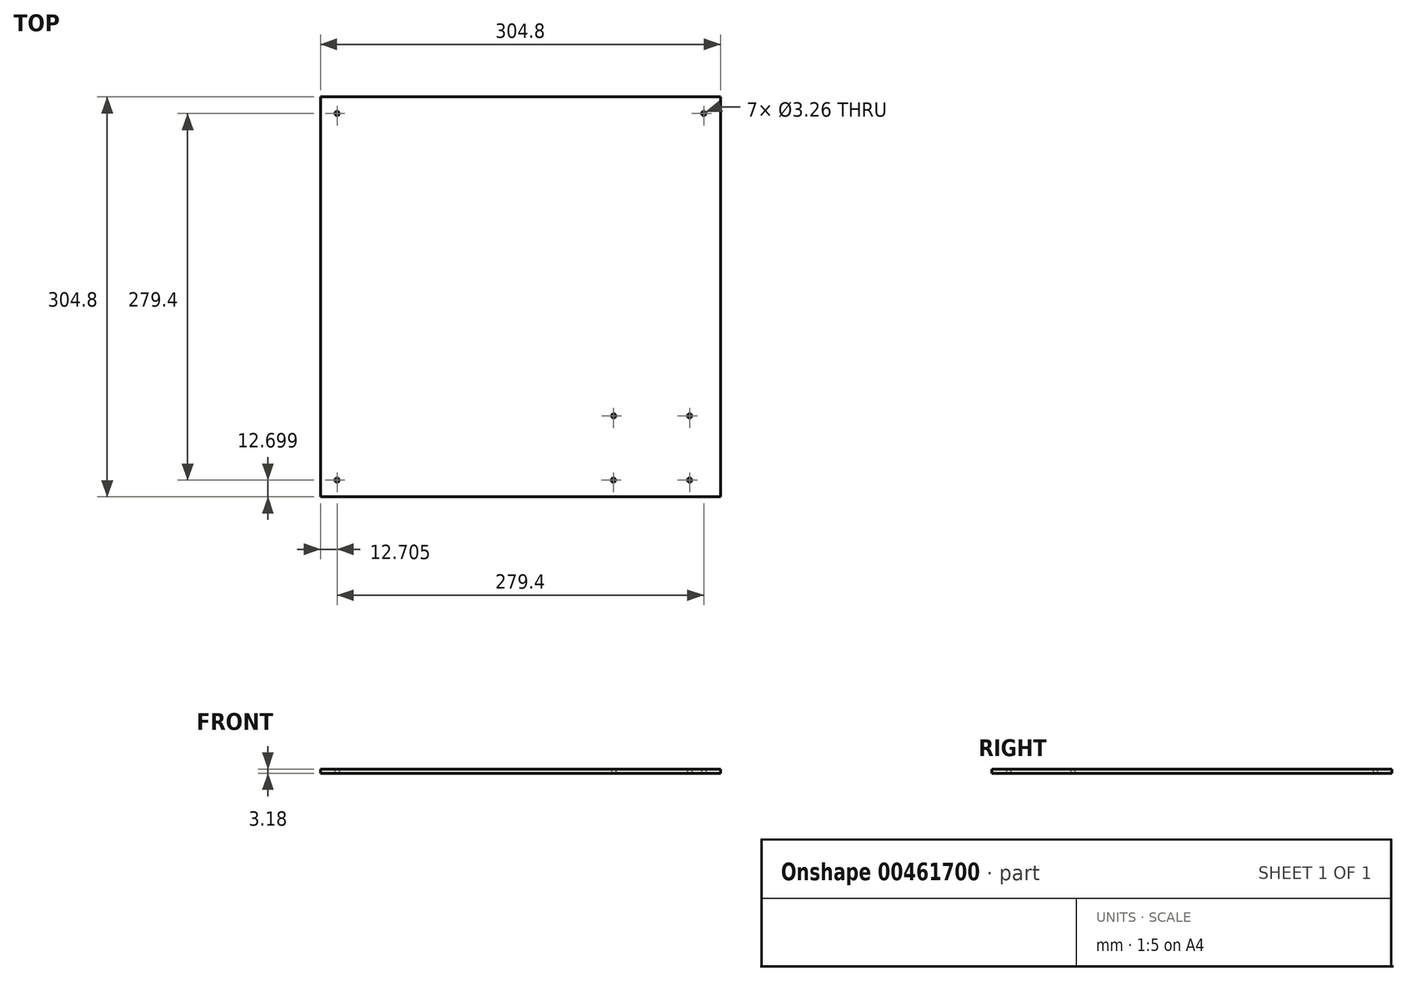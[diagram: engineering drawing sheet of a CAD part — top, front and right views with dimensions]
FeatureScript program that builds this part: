
annotation { "Feature Type Name" : "Feature", "Feature Type Description" : "" }
export const myFeature = defineFeature(function(context is Context, id is Id, definition is map)
    precondition{}
    {
        {
            var Q0;
            Q0=qCreatedBy(makeId("Top.planeOp"),FACE);
            var sketch = newSketch(context, id + "F0", { "sketchPlane" : qUnion([Q0])});
            skLineSegment(sketch, "E0.bottom", {"start": v(-241.1, 248.87) * mm, "end": v(63.7, 248.87) * mm});
            skLineSegment(sketch, "E0.top", {"start": v(-241.1, -55.93) * mm, "end": v(63.7, -55.93) * mm});
            skLineSegment(sketch, "E0.left", {"start": v(-241.1, 248.87) * mm, "end": v(-241.1, -55.93) * mm});
            skLineSegment(sketch, "E0.right", {"start": v(63.7, 248.87) * mm, "end": v(63.7, -55.93) * mm});
            skCircle(sketch, "E1", {"center": v(-228.4, 236.17) * mm, "radius": 1.63 * mm});
            skCircle(sketch, "E2", {"center": v(51, 236.17) * mm, "radius": 1.63 * mm});
            skCircle(sketch, "E3", {"center": v(-228.4, -43.23) * mm, "radius": 1.63 * mm});
            skCircle(sketch, "E4", {"center": v(40.2, -43.23) * mm, "radius": 1.63 * mm});
            skCircle(sketch, "E5", {"center": v(-17.8, -43.23) * mm, "radius": 1.63 * mm});
            skCircle(sketch, "E6", {"center": v(40.2, 5.77) * mm, "radius": 1.63 * mm});
            skCircle(sketch, "E7", {"center": v(-17.6, 5.77) * mm, "radius": 1.63 * mm});
            skSolve(sketch);
        }
        {
            var Q0;
            Q0=makeQuery(id+"F0.imprint","IMPRINT",FACE,{"disambiguationData":[TD([[makeQuery(id+"F0.imprint","IMPRINT",EDGE,{"derivedFrom":sQuery(id+"F0.wireOp",EDGE,"E0.bottom")}),-1.0]])]});
            extrude(context, id + "F1", {"entities" : qUnion([Q0]), "depth" : 3.17 * mm});
        }
    });
